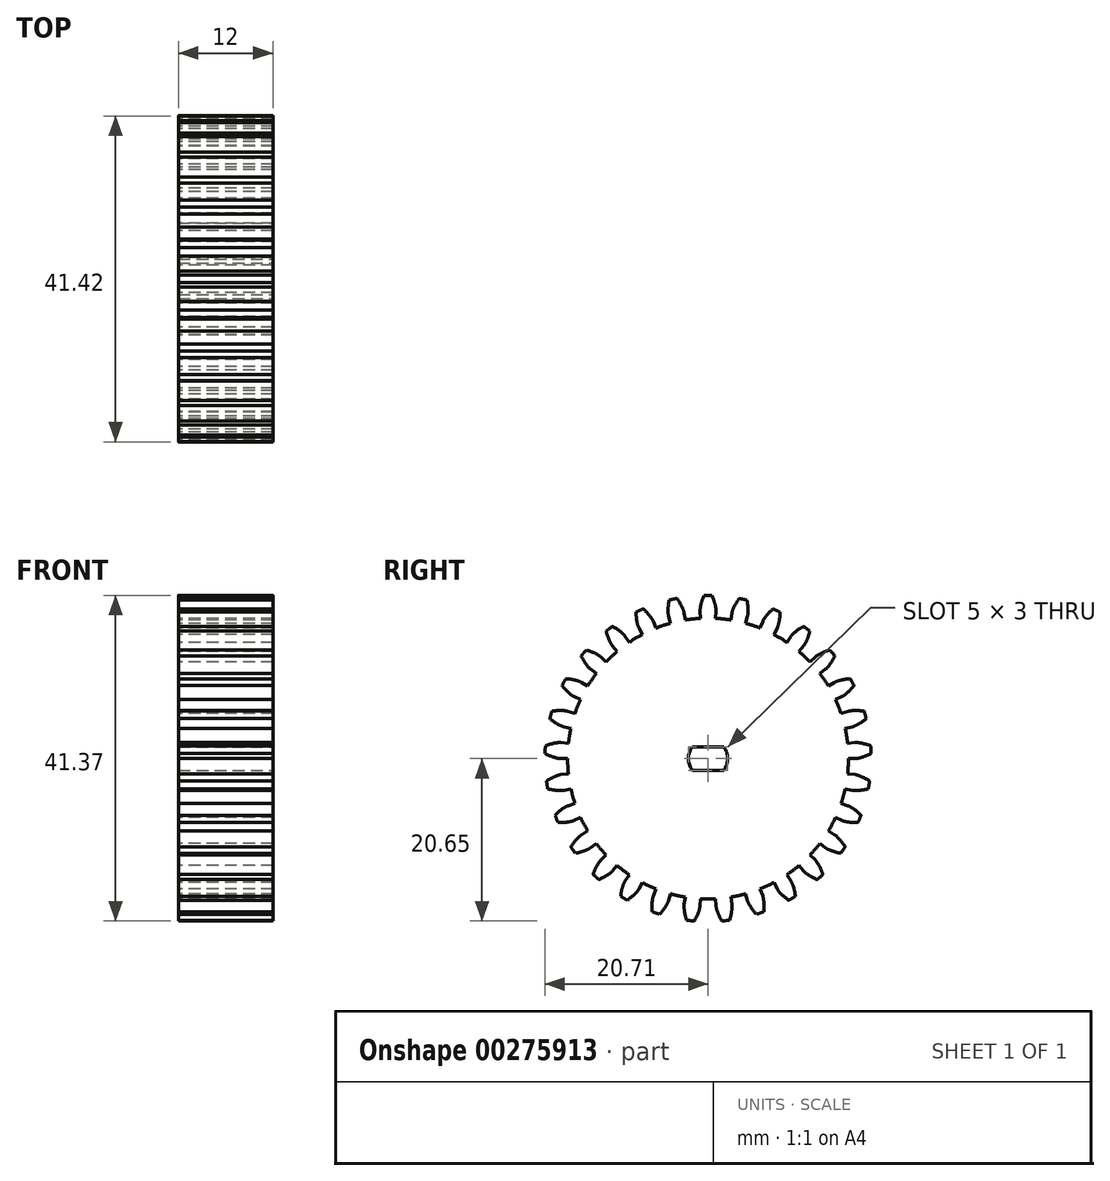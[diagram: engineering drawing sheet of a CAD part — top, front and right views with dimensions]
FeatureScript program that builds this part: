
annotation { "Feature Type Name" : "Feature", "Feature Type Description" : "" }
export const myFeature = defineFeature(function(context is Context, id is Id, definition is map)
    precondition{}
    {
        {
            assignVariable(context, id + "F0", {"name" : "NumberTeeth", "anyValue" : 29});
        }
        {
            assignVariable(context, id + "F1", {"name" : "GearThickness", "anyValue" : 12});
        }
        {
            var Q0;
            Q0=qCreatedBy(makeId("Right.planeOp"),FACE);
            var sketch = newSketch(context, id + "F2", { "sketchPlane" : qUnion([Q0])});
            skCircle(sketch, "E0", {"center": v(0, 0) * mm, "radius": 17.84 * mm});
            skCircle(sketch, "E1", {"center": v(0, 0) * mm, "radius": 18.77 * mm, "construction": true});
            skCircle(sketch, "E2", {"center": v(0, 0) * mm, "radius": 19.38 * mm, "construction": true});
            skCircle(sketch, "E3", {"center": v(0, 0) * mm, "radius": 20.72 * mm});
            skLineSegment(sketch, "E4", {"start": v(0, 0) * mm, "end": v(-18.77, 0) * mm, "construction": true});
            skLineSegment(sketch, "E5.1.0", {"start": v(0, 0) * mm, "end": v(-18.74, 0.94) * mm, "construction": true});
            skLineSegment(sketch, "E5.2.0", {"start": v(0, 0) * mm, "end": v(-18.67, 1.87) * mm, "construction": true});
            skLineSegment(sketch, "E5.3.0", {"start": v(0, 0) * mm, "end": v(-18.56, 2.8) * mm, "construction": true});
            skLineSegment(sketch, "E5.4.0", {"start": v(0, 0) * mm, "end": v(-18.4, 3.73) * mm, "construction": true});
            skLineSegment(sketch, "E5.5.0", {"start": v(0, 0) * mm, "end": v(-18.18, 4.64) * mm, "construction": true});
            skLineSegment(sketch, "E5.6.0", {"start": v(0, 0) * mm, "end": v(-17.93, 5.55) * mm, "construction": true});
            skLineSegment(sketch, "E5.7.0", {"start": v(0, 0) * mm, "end": v(-17.63, 6.44) * mm, "construction": true});
            skLineSegment(sketch, "E5.8.0", {"start": v(0, 0) * mm, "end": v(-17.29, 7.3) * mm, "construction": true});
            skLineSegment(sketch, "E5.9.0", {"start": v(0, 0) * mm, "end": v(-16.9, 8.16) * mm, "construction": true});
            skLineSegment(sketch, "E5.10.0", {"start": v(0, 0) * mm, "end": v(-16.47, 9) * mm, "construction": true});
            skLineSegment(sketch, "E5.11.0", {"start": v(0, 0) * mm, "end": v(-16, 9.8) * mm, "construction": true});
            skLineSegment(sketch, "E5.12.0", {"start": v(0, 0) * mm, "end": v(-15.49, 10.6) * mm, "construction": true});
            skLineSegment(sketch, "E5.13.0", {"start": v(0, 0) * mm, "end": v(-14.94, 11.36) * mm, "construction": true});
            skLineSegment(sketch, "E5.14.0", {"start": v(0, 0) * mm, "end": v(-14.35, 12.09) * mm, "construction": true});
            skLineSegment(sketch, "E5.anchor2", {"start": v(0, 0) * mm, "end": v(-14.35, 12.09) * mm, "construction": true});
            skLineSegment(sketch, "E6", {"start": v(-18.74, 0.94) * mm, "end": v(-18.8, 0) * mm, "construction": true});
            skLineSegment(sketch, "E7", {"start": v(-18.67, 1.87) * mm, "end": v(-18.86, 0) * mm, "construction": true});
            skLineSegment(sketch, "E8", {"start": v(-18.56, 2.8) * mm, "end": v(-18.98, 0.02) * mm, "construction": true});
            skLineSegment(sketch, "E9", {"start": v(-18.18, 4.64) * mm, "end": v(-19.34, 0.1) * mm, "construction": true});
            skLineSegment(sketch, "E10", {"start": v(-17.93, 5.55) * mm, "end": v(-19.6, 0.17) * mm, "construction": true});
            skLineSegment(sketch, "E11", {"start": v(-17.63, 6.44) * mm, "end": v(-19.88, 0.26) * mm, "construction": true});
            skLineSegment(sketch, "E12", {"start": v(-17.29, 7.3) * mm, "end": v(-20.2, 0.4) * mm, "construction": true});
            skLineSegment(sketch, "E13", {"start": v(-16.9, 8.16) * mm, "end": v(-20.57, 0.56) * mm, "construction": true});
            skLineSegment(sketch, "E14", {"start": v(-16.47, 9) * mm, "end": v(-20.97, 0.76) * mm, "construction": true});
            skLineSegment(sketch, "E15", {"start": v(-16, 9.8) * mm, "end": v(-21.4, 1) * mm, "construction": true});
            skLineSegment(sketch, "E16", {"start": v(-18.4, 3.73) * mm, "end": v(-19.14, 0.05) * mm, "construction": true});
            skLineSegment(sketch, "E17", {"start": v(-15.49, 10.6) * mm, "end": v(-21.85, 1.3) * mm, "construction": true});
            skLineSegment(sketch, "E18", {"start": v(-14.94, 11.36) * mm, "end": v(-22.32, 1.65) * mm, "construction": true});
            skLineSegment(sketch, "E19", {"start": v(-14.35, 12.09) * mm, "end": v(-22.82, 2.04) * mm, "construction": true});
            skLineSegment(sketch, "E20", {"start": v(0, 0) * mm, "end": v(-18.74, 1.02) * mm, "construction": true});
            skLineSegment(sketch, "E21", {"start": v(-17.84, 0) * mm, "end": v(-18.77, 0) * mm});
            skLineSegment(sketch, "E22.MirrorCS", {"start": v(-17.73, 1.93) * mm, "end": v(-18.66, 2.03) * mm});
            skFitSpline(sketch, "E23", {"points": [v(-18.77, 0) * mm, v(-18.8, 0) * mm, v(-18.86, 0) * mm, v(-18.98, 0.02) * mm, v(-19.14, 0.05) * mm, v(-19.34, 0.1) * mm, v(-19.6, 0.17) * mm, v(-19.88, 0.26) * mm, v(-20.2, 0.4) * mm, v(-20.57, 0.56) * mm, v(-20.97, 0.76) * mm, v(-21.4, 1) * mm, v(-21.85, 1.3) * mm, v(-22.32, 1.65) * mm, v(-22.82, 2.04) * mm], "startDerivative": vector(-0.8, 0) * mm, "endDerivative": vector(-1.29, 1.09) * mm});
            skLineSegment(sketch, "E24", {"start": v(-20.57, 0.15) * mm, "end": v(-22.82, 2.04) * mm, "construction": true});
            skFitSpline(sketch, "E25.MirrorCS", {"points": [v(-18.66, 2.03) * mm, v(-18.68, 2.03) * mm, v(-18.75, 2.03) * mm, v(-18.87, 2.03) * mm, v(-19.03, 2.02) * mm, v(-19.24, 2) * mm, v(-19.5, 1.95) * mm, v(-19.8, 1.89) * mm, v(-20.13, 1.8) * mm, v(-20.51, 1.67) * mm, v(-20.93, 1.5) * mm, v(-21.38, 1.3) * mm, v(-21.86, 1.07) * mm, v(-22.37, 0.78) * mm, v(-22.9, 0.44) * mm], "startDerivative": vector(-0.79, 0.09) * mm, "endDerivative": vector(-1.4, -0.94) * mm});
            skSolve(sketch);
        }
        {
            var Q0;
            {var subQ0=sQuery(id+"F2.wireOp",EDGE,"E0");var subQ27=makeQuery(id+"F2.imprint","INTERSECT",VERTEX,{"derivedFrom":[subQ0,sQuery(id+"F2.wireOp",EDGE,"10ea1024-8cf5-41f5-a75f-a634b86921f3.10.0")]});Q0=makeQuery(id+"F2.imprint","IMPRINT",FACE,{"disambiguationData":[TD([[makeQuery(id+"F2.imprint","IMPRINT",EDGE,{"disambiguationData":[TD([[subQ27,-1.0]])],"derivedFrom":subQ0}),1.0]])]});}
            var Q1;
            {var subQ0=sQuery(id+"F2.wireOp",EDGE,"10ea1024-8cf5-41f5-a75f-a634b86921f3.1.0");Q1=makeQuery(id+"F2.imprint","IMPRINT",FACE,{"disambiguationData":[TD([[makeQuery(id+"F2.imprint","IMPRINT",EDGE,{"derivedFrom":subQ0}),-1.0]])]});}
            var Q2;
            {var subQ7=sQuery(id+"F2.wireOp",EDGE,"10ea1024-8cf5-41f5-a75f-a634b86921f3.2.0");Q2=makeQuery(id+"F2.imprint","IMPRINT",FACE,{"disambiguationData":[TD([[makeQuery(id+"F2.imprint","IMPRINT",EDGE,{"derivedFrom":subQ7}),-1.0]])]});}
            var Q3;
            {var subQ8=sQuery(id+"F2.wireOp",EDGE,"10ea1024-8cf5-41f5-a75f-a634b86921f3.3.0");Q3=makeQuery(id+"F2.imprint","IMPRINT",FACE,{"disambiguationData":[TD([[makeQuery(id+"F2.imprint","IMPRINT",EDGE,{"derivedFrom":subQ8}),-1.0]])]});}
            var Q4;
            {var subQ2=sQuery(id+"F2.wireOp",EDGE,"10ea1024-8cf5-41f5-a75f-a634b86921f3.4.0");Q4=makeQuery(id+"F2.imprint","IMPRINT",FACE,{"disambiguationData":[TD([[makeQuery(id+"F2.imprint","IMPRINT",EDGE,{"derivedFrom":subQ2}),-1.0]])]});}
            var Q5;
            {var subQ8=sQuery(id+"F2.wireOp",EDGE,"10ea1024-8cf5-41f5-a75f-a634b86921f3.5.0");Q5=makeQuery(id+"F2.imprint","IMPRINT",FACE,{"disambiguationData":[TD([[makeQuery(id+"F2.imprint","IMPRINT",EDGE,{"derivedFrom":subQ8}),-1.0]])]});}
            var Q6;
            {var subQ3=sQuery(id+"F2.wireOp",EDGE,"10ea1024-8cf5-41f5-a75f-a634b86921f3.6.0");Q6=makeQuery(id+"F2.imprint","IMPRINT",FACE,{"disambiguationData":[TD([[makeQuery(id+"F2.imprint","IMPRINT",EDGE,{"derivedFrom":subQ3}),-1.0]])]});}
            var Q7;
            {var subQ0=sQuery(id+"F2.wireOp",EDGE,"10ea1024-8cf5-41f5-a75f-a634b86921f3.7.0");Q7=makeQuery(id+"F2.imprint","IMPRINT",FACE,{"disambiguationData":[TD([[makeQuery(id+"F2.imprint","IMPRINT",EDGE,{"derivedFrom":subQ0}),-1.0]])]});}
            var Q8;
            {var subQ5=sQuery(id+"F2.wireOp",EDGE,"10ea1024-8cf5-41f5-a75f-a634b86921f3.8.0");Q8=makeQuery(id+"F2.imprint","IMPRINT",FACE,{"disambiguationData":[TD([[makeQuery(id+"F2.imprint","IMPRINT",EDGE,{"derivedFrom":subQ5}),-1.0]])]});}
            var Q9;
            {var subQ1=sQuery(id+"F2.wireOp",EDGE,"10ea1024-8cf5-41f5-a75f-a634b86921f3.9.0");Q9=makeQuery(id+"F2.imprint","IMPRINT",FACE,{"disambiguationData":[TD([[makeQuery(id+"F2.imprint","IMPRINT",EDGE,{"derivedFrom":subQ1}),-1.0]])]});}
            var Q10;
            {var subQ5=sQuery(id+"F2.wireOp",EDGE,"10ea1024-8cf5-41f5-a75f-a634b86921f3.10.0");Q10=makeQuery(id+"F2.imprint","IMPRINT",FACE,{"disambiguationData":[TD([[makeQuery(id+"F2.imprint","IMPRINT",EDGE,{"derivedFrom":subQ5}),-1.0]])]});}
            var Q11;
            {var subQ8=sQuery(id+"F2.wireOp",EDGE,"10ea1024-8cf5-41f5-a75f-a634b86921f3.11.0");Q11=makeQuery(id+"F2.imprint","IMPRINT",FACE,{"disambiguationData":[TD([[makeQuery(id+"F2.imprint","IMPRINT",EDGE,{"derivedFrom":subQ8}),-1.0]])]});}
            var Q12;
            {var subQ2=sQuery(id+"F2.wireOp",EDGE,"10ea1024-8cf5-41f5-a75f-a634b86921f3.12.0");Q12=makeQuery(id+"F2.imprint","IMPRINT",FACE,{"disambiguationData":[TD([[makeQuery(id+"F2.imprint","IMPRINT",EDGE,{"derivedFrom":subQ2}),-1.0]])]});}
            var Q13;
            {var subQ3=sQuery(id+"F2.wireOp",EDGE,"10ea1024-8cf5-41f5-a75f-a634b86921f3.13.0");Q13=makeQuery(id+"F2.imprint","IMPRINT",FACE,{"disambiguationData":[TD([[makeQuery(id+"F2.imprint","IMPRINT",EDGE,{"derivedFrom":subQ3}),-1.0]])]});}
            var Q14;
            {var subQ0=sQuery(id+"F2.wireOp",EDGE,"10ea1024-8cf5-41f5-a75f-a634b86921f3.14.0");Q14=makeQuery(id+"F2.imprint","IMPRINT",FACE,{"disambiguationData":[TD([[makeQuery(id+"F2.imprint","IMPRINT",EDGE,{"derivedFrom":subQ0}),-1.0]])]});}
            var Q15;
            {var subQ6=sQuery(id+"F2.wireOp",EDGE,"10ea1024-8cf5-41f5-a75f-a634b86921f3.15.0");Q15=makeQuery(id+"F2.imprint","IMPRINT",FACE,{"disambiguationData":[TD([[makeQuery(id+"F2.imprint","IMPRINT",EDGE,{"derivedFrom":subQ6}),-1.0]])]});}
            var Q16;
            {var subQ5=sQuery(id+"F2.wireOp",EDGE,"10ea1024-8cf5-41f5-a75f-a634b86921f3.16.0");Q16=makeQuery(id+"F2.imprint","IMPRINT",FACE,{"disambiguationData":[TD([[makeQuery(id+"F2.imprint","IMPRINT",EDGE,{"derivedFrom":subQ5}),-1.0]])]});}
            var Q17;
            {var subQ7=sQuery(id+"F2.wireOp",EDGE,"10ea1024-8cf5-41f5-a75f-a634b86921f3.17.0");Q17=makeQuery(id+"F2.imprint","IMPRINT",FACE,{"disambiguationData":[TD([[makeQuery(id+"F2.imprint","IMPRINT",EDGE,{"derivedFrom":subQ7}),-1.0]])]});}
            var Q18;
            {var subQ5=sQuery(id+"F2.wireOp",EDGE,"10ea1024-8cf5-41f5-a75f-a634b86921f3.18.0");Q18=makeQuery(id+"F2.imprint","IMPRINT",FACE,{"disambiguationData":[TD([[makeQuery(id+"F2.imprint","IMPRINT",EDGE,{"derivedFrom":subQ5}),-1.0]])]});}
            var Q19;
            {var subQ8=sQuery(id+"F2.wireOp",EDGE,"10ea1024-8cf5-41f5-a75f-a634b86921f3.19.0");Q19=makeQuery(id+"F2.imprint","IMPRINT",FACE,{"disambiguationData":[TD([[makeQuery(id+"F2.imprint","IMPRINT",EDGE,{"derivedFrom":subQ8}),-1.0]])]});}
            var Q20;
            {var subQ8=sQuery(id+"F2.wireOp",EDGE,"E21");Q20=makeQuery(id+"F2.imprint","IMPRINT",FACE,{"disambiguationData":[TD([[makeQuery(id+"F2.imprint","IMPRINT",EDGE,{"derivedFrom":subQ8}),-1.0]])]});}
            extrude(context, id + "F3", {"entities" : qUnion([Q0, Q1, Q2, Q3, Q4, Q5, Q6, Q7, Q8, Q9, Q10, Q11, Q12, Q13, Q14, Q15, Q16, Q17, Q18, Q19, Q20]), "depth" : (getVariable(context, 'GearThickness')) * mm});
        }
        {
            var Q0;
            Q0=makeQuery(id+"F3.opExtrude","SWEPT_FACE",FACE,{"disambiguationData":[OSD([sQuery(id+"F2.wireOp",EDGE,"E25.MirrorCS")])]});
            var Q1;
            Q1=makeQuery(id+"F3.opExtrude","SWEPT_FACE",FACE,{"disambiguationData":[OSD([sQuery(id+"F2.wireOp",EDGE,"E23")])]});
            var Q2;
            Q2=makeQuery(id+"F3.opExtrude","SWEPT_FACE",FACE,{"disambiguationData":[OSD([sQuery(id+"F2.wireOp",EDGE,"E3")])]});
            var Q3;
            Q3=makeQuery(id+"F3.opExtrude","SWEPT_FACE",FACE,{"disambiguationData":[OSD([sQuery(id+"F2.wireOp",EDGE,"E22.MirrorCS")])]});
            var Q4;
            Q4=makeQuery(id+"F3.opExtrude","SWEPT_FACE",FACE,{"disambiguationData":[OSD([sQuery(id+"F2.wireOp",EDGE,"E21")])]});
            var Q5;
            Q5=makeQuery(id+"F3.opExtrude","SWEPT_FACE",FACE,{"disambiguationData":[OSD([sQuery(id+"F2.wireOp",EDGE,"E0")])]});
            circularPattern(context, id + "F4", {"faces" : qUnion([Q0, Q1, Q2, Q3, Q4]), "axis" : qUnion([Q5]), "angle" : 360 * degree, "instanceCount" : getVariable(context, 'NumberTeeth'), "equalSpace" : true, "patternType" : PatternType.FACE});
        }
        {
            var Q0;
            Q0=makeQuery(id+"F3.opExtrude","CAP_FACE",FACE,{"disambiguationData":[OSD([sQuery(id+"F2.wireOp",EDGE,"E0"),sQuery(id+"F2.wireOp",EDGE,"E3"),sQuery(id+"F2.wireOp",EDGE,"E21"),sQuery(id+"F2.wireOp",EDGE,"E22.MirrorCS"),sQuery(id+"F2.wireOp",EDGE,"E23"),sQuery(id+"F2.wireOp",EDGE,"E25.MirrorCS")])],"isStart":false});
            var sketch = newSketch(context, id + "F5", { "sketchPlane" : qUnion([Q0])});
            skCircle(sketch, "E26", {"center": v(0, 0) * mm, "radius": 2.5 * mm, "construction": true});
            skLineSegment(sketch, "E27.bottom", {"start": v(-2.5, 1.5) * mm, "end": v(2.5, 1.5) * mm, "construction": true});
            skLineSegment(sketch, "E27.top", {"start": v(-2.5, -1.5) * mm, "end": v(2.5, -1.5) * mm, "construction": true});
            skLineSegment(sketch, "E27.left", {"start": v(-2.5, 1.5) * mm, "end": v(-2.5, -1.5) * mm, "construction": true});
            skLineSegment(sketch, "E27.right", {"start": v(2.5, 1.5) * mm, "end": v(2.5, -1.5) * mm, "construction": true});
            skLineSegment(sketch, "E28", {"start": v(-2, 1.5) * mm, "end": v(2, 1.5) * mm});
            skLineSegment(sketch, "E29", {"start": v(-2, -1.5) * mm, "end": v(2, -1.5) * mm});
            skArc(sketch, "E30", {"start": v(-2, 1.5) * mm, "mid": v(-2.5, 0) * mm, "end": v(-2, -1.5) * mm});
            skArc(sketch, "E31", {"start": v(2, 1.5) * mm, "mid": v(2.5, 0) * mm, "end": v(2, -1.5) * mm});
            skSolve(sketch);
        }
        {
            var Q0;
            Q0 = qSketchRegion(id + "F5", true);
            extrude(context, id + "F6", {"entities" : qUnion([Q0]), "operationType" : NewBodyOperationType.REMOVE, "endBound" : BoundingType.THROUGH_ALL, "oppositeDirection" : true, "depth" : 25 * mm});
        }
    });
